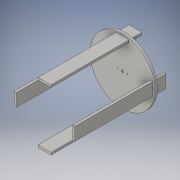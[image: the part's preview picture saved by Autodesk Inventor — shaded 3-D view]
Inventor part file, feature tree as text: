
AUTODESK INVENTOR PART (.ipt)
format: ipt  version: 2016 (Build 200138000, 138)  size: 144,896 bytes
history: native  units: in
note: dims shown in document units (in); Inventor stores cm internally (conversion verified against a paired STEP export)
features: extrude x2, sketch x2
ambient origin geometry x8: Origin, YZ Plane, XZ Plane, XY Plane, X Axis, Y Axis, Z Axis, Center Point
bodies: Solid1 (feature_tree)
feature tree (4):
  extrude  "Extrusion1"  Depth=0.375in
  extrude  "Extrusion2"  Depth=1.0in
  sketch  "Sketch1"  dims[d0=5.0in d2=0.375in]
  sketch  "Sketch2"  dims[d3=0.375in d4=0.075in d5=0.075in d6=0.175in d7=0.18in d8=0.0in d10=2.25in d11=2.25in d12=2.25in d13=180.0deg d14=2.25in d15=0.18in d16=1.0in d17=1.0in d18=0.18in d19=0.18in d20=1.0in d21=0.18in d22=6.0in d23=1.0in d24=0.0in d25=0.0in]
